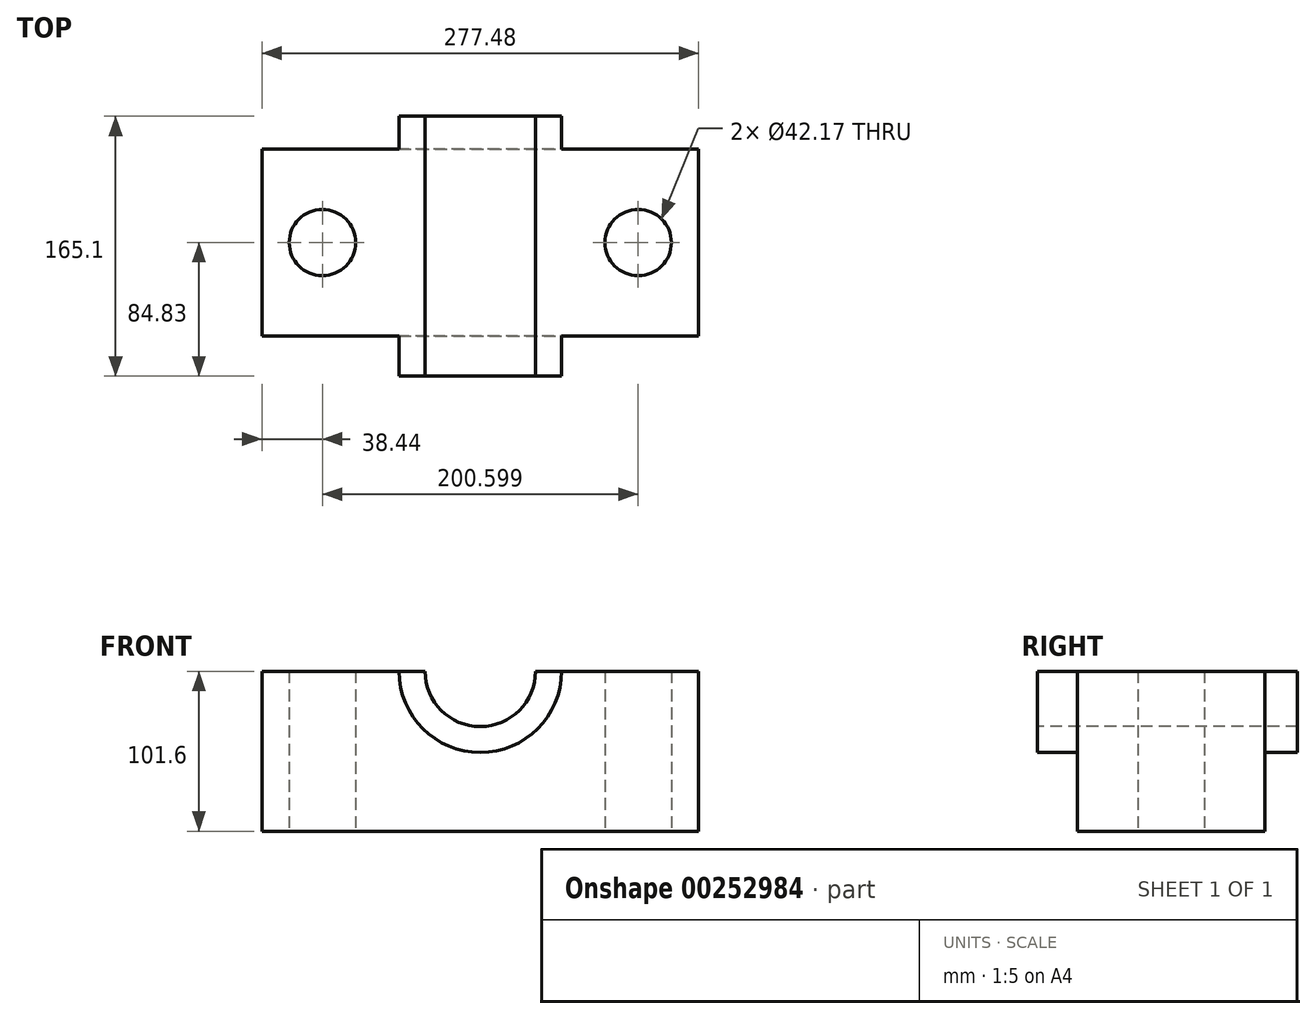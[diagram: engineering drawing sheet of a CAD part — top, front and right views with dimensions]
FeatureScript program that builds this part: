
annotation { "Feature Type Name" : "Feature", "Feature Type Description" : "" }
export const myFeature = defineFeature(function(context is Context, id is Id, definition is map)
    precondition{}
    {
        {
            var Q0;
            Q0=qCreatedBy(makeId("Top.planeOp"),FACE);
            var sketch = newSketch(context, id + "F0", { "sketchPlane" : qUnion([Q0])});
            skLineSegment(sketch, "E0.bottom", {"start": v(138.74, 59.43) * mm, "end": v(-138.74, 59.43) * mm});
            skLineSegment(sketch, "E0.top", {"start": v(138.74, -59.43) * mm, "end": v(-138.74, -59.43) * mm});
            skLineSegment(sketch, "E0.left", {"start": v(138.74, 59.43) * mm, "end": v(138.74, -59.43) * mm});
            skLineSegment(sketch, "E0.right", {"start": v(-138.74, 59.43) * mm, "end": v(-138.74, -59.43) * mm});
            skPoint(sketch, "E0.middle", {"position": v(0, 0) * mm});
            skCircle(sketch, "E1", {"center": v(-100.3, 0) * mm, "radius": 21.09 * mm});
            skCircle(sketch, "E2.MirrorC", {"center": v(100.3, 0) * mm, "radius": 21.09 * mm});
            skSolve(sketch);
        }
        {
            var Q0;
            Q0=qSketchRegion(id+"F0",true);
            extrude(context, id + "F1", {"entities" : qUnion([Q0]), "depth" : 101.6 * mm});
        }
        {
            var Q0;
            Q0=makeQuery(id+"F1.opExtrude","SWEPT_FACE",FACE,{"disambiguationData":[OSD([sQuery(id+"F0.wireOp",EDGE,"E0.top")])]});
            var sketch = newSketch(context, id + "F2", { "sketchPlane" : qUnion([Q0])});
            skCircle(sketch, "E3", {"center": v(0, 101.6) * mm, "radius": 35.08 * mm});
            skSolve(sketch);
        }
        {
            var Q0;
            Q0=qSketchRegion(id+"F2",true);
            extrude(context, id + "F3", {"entities" : qUnion([Q0]), "operationType" : NewBodyOperationType.REMOVE, "endBound" : BoundingType.THROUGH_ALL, "oppositeDirection" : true, "depth" : 25.4 * mm});
        }
        {
            var Q0;
            Q0=makeQuery(id+"F1.opExtrude","SWEPT_FACE",FACE,{"disambiguationData":[OSD([sQuery(id+"F0.wireOp",EDGE,"E0.top")])]});
            var sketch = newSketch(context, id + "F4", { "sketchPlane" : qUnion([Q0])});
            skArc(sketch, "E4.0", {"start": v(-35.08, 101.6) * mm, "mid": v(0, 66.52) * mm, "end": v(35.08, 101.6) * mm});
            skLineSegment(sketch, "E5.0", {"start": v(138.74, 101.6) * mm, "end": v(35.08, 101.6) * mm});
            skLineSegment(sketch, "E6.0", {"start": v(-35.08, 101.6) * mm, "end": v(-138.74, 101.6) * mm});
            skLineSegment(sketch, "E7.0", {"start": v(138.74, 0) * mm, "end": v(-138.74, 0) * mm});
            skLineSegment(sketch, "E8.0", {"start": v(138.74, 101.6) * mm, "end": v(138.74, 0) * mm});
            skLineSegment(sketch, "E9.0", {"start": v(-138.74, 101.6) * mm, "end": v(-138.74, 0) * mm});
            skArc(sketch, "E10", {"start": v(-51.58, 101.6) * mm, "mid": v(0, 50.02) * mm, "end": v(51.58, 101.6) * mm});
            skSolve(sketch);
        }
        {
            var Q0;
            {var subQ0=sQuery(id+"F4.wireOp",EDGE,"E4.0");Q0=makeQuery(id+"F4.imprint","IMPRINT",FACE,{"disambiguationData":[TD([[makeQuery(id+"F4.imprint","IMPRINT",EDGE,{"derivedFrom":subQ0}),-1.0]])]});}
            extrude(context, id + "F5", {"entities" : qUnion([Q0]), "operationType" : NewBodyOperationType.ADD, "depth" : 25.4 * mm, "hasSecondDirection" : true, "secondDirectionOppositeDirection" : true, "secondDirectionDepth" : 139.7 * mm});
        }
    });
